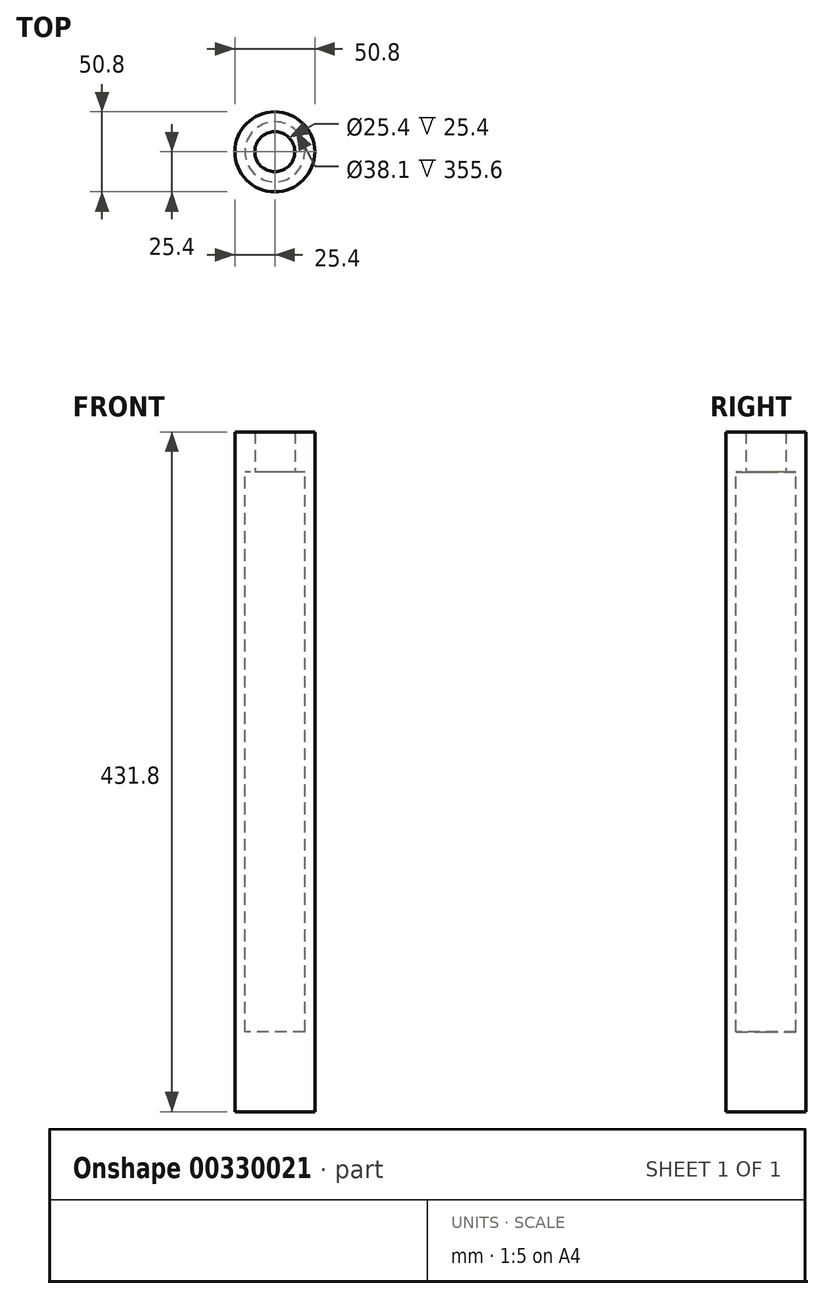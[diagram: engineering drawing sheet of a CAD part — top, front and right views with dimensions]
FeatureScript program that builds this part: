
annotation { "Feature Type Name" : "Feature", "Feature Type Description" : "" }
export const myFeature = defineFeature(function(context is Context, id is Id, definition is map)
    precondition{}
    {
        {
            var Q0;
            Q0=qCreatedBy(makeId("Top.planeOp"),FACE);
            var sketch = newSketch(context, id + "F0", { "sketchPlane" : qUnion([Q0])});
            skCircle(sketch, "E0", {"center": v(0, 0) * mm, "radius": 25.4 * mm});
            skSolve(sketch);
        }
        {
            var Q0;
            Q0 = qSketchRegion(id + "F0", true);
            extrude(context, id + "F1", {"entities" : qUnion([Q0]), "oppositeDirection" : true, "depth" : 406.4 * mm, "hasSecondDirection" : true, "secondDirectionOppositeDirection" : false, "secondDirectionDepth" : 25.4 * mm});
        }
        {
            var Q0;
            Q0=qCreatedBy(makeId("Top.planeOp"),FACE);
            var sketch = newSketch(context, id + "F2", { "sketchPlane" : qUnion([Q0])});
            skCircle(sketch, "E1", {"center": v(0, 0) * mm, "radius": 19.05 * mm});
            skSolve(sketch);
        }
        {
            var Q0;
            Q0 = qSketchRegion(id + "F2", true);
            extrude(context, id + "F3", {"entities" : qUnion([Q0]), "operationType" : NewBodyOperationType.REMOVE, "oppositeDirection" : true, "depth" : 355.6 * mm});
        }
        {
            var Q0;
            Q0=qCreatedBy(makeId("Top.planeOp"),FACE);
            var sketch = newSketch(context, id + "F4", { "sketchPlane" : qUnion([Q0])});
            skCircle(sketch, "E2", {"center": v(0, 0) * mm, "radius": 12.7 * mm});
            skSolve(sketch);
        }
        {
            var Q0;
            Q0 = qSketchRegion(id + "F4", true);
            extrude(context, id + "F5", {"entities" : qUnion([Q0]), "operationType" : NewBodyOperationType.REMOVE, "endBound" : BoundingType.THROUGH_ALL, "depth" : 25.4 * mm});
        }
    });
